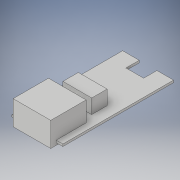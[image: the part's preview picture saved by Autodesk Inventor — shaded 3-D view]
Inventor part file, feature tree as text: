
AUTODESK INVENTOR PART (.ipt)
format: ipt  version: 2018 (Build 220112000, 112)  size: 146,432 bytes
history: native  units: in
note: dims shown in document units (in); Inventor stores cm internally (conversion verified against a paired STEP export)
features: extrude x5, sketch x5
ambient origin geometry x8: Origin, YZ Plane, XZ Plane, XY Plane, X Axis, Y Axis, Z Axis, Center Point
bodies: Solid1 (feature_tree)
feature tree (10):
  extrude  "Extrusion1"  Depth=0.9055in
  extrude  "Extrusion2"  Depth=0.0984in
  extrude  "Extrusion3"  Depth=0.6299in
  extrude  "Extrusion4"  Depth=0.0787in TaperAngle=0.0deg
  extrude  "Extrusion5"  Depth=0.2756in
  sketch  "Sketch1"  dims[d0=1.9685in d1=0.9055in]
  sketch  "Sketch2"  dims[d2=0.0394in d3=0.0in d4=0.0984in]
  sketch  "Sketch3"  dims[d5=0.6693in d6=0.6299in]
  sketch  "Sketch4"  dims[d7=0.3543in d8=0.0in d9=0.0787in d10=0.0in]
  sketch  "Sketch5"  dims[d11=0.1772in d12=0.2756in d13=0.5118in d14=0.2559in d15=0.0in d16=0.0in d17=0.315in d18=0.2362in d19=0.2559in d20=0.0in]
